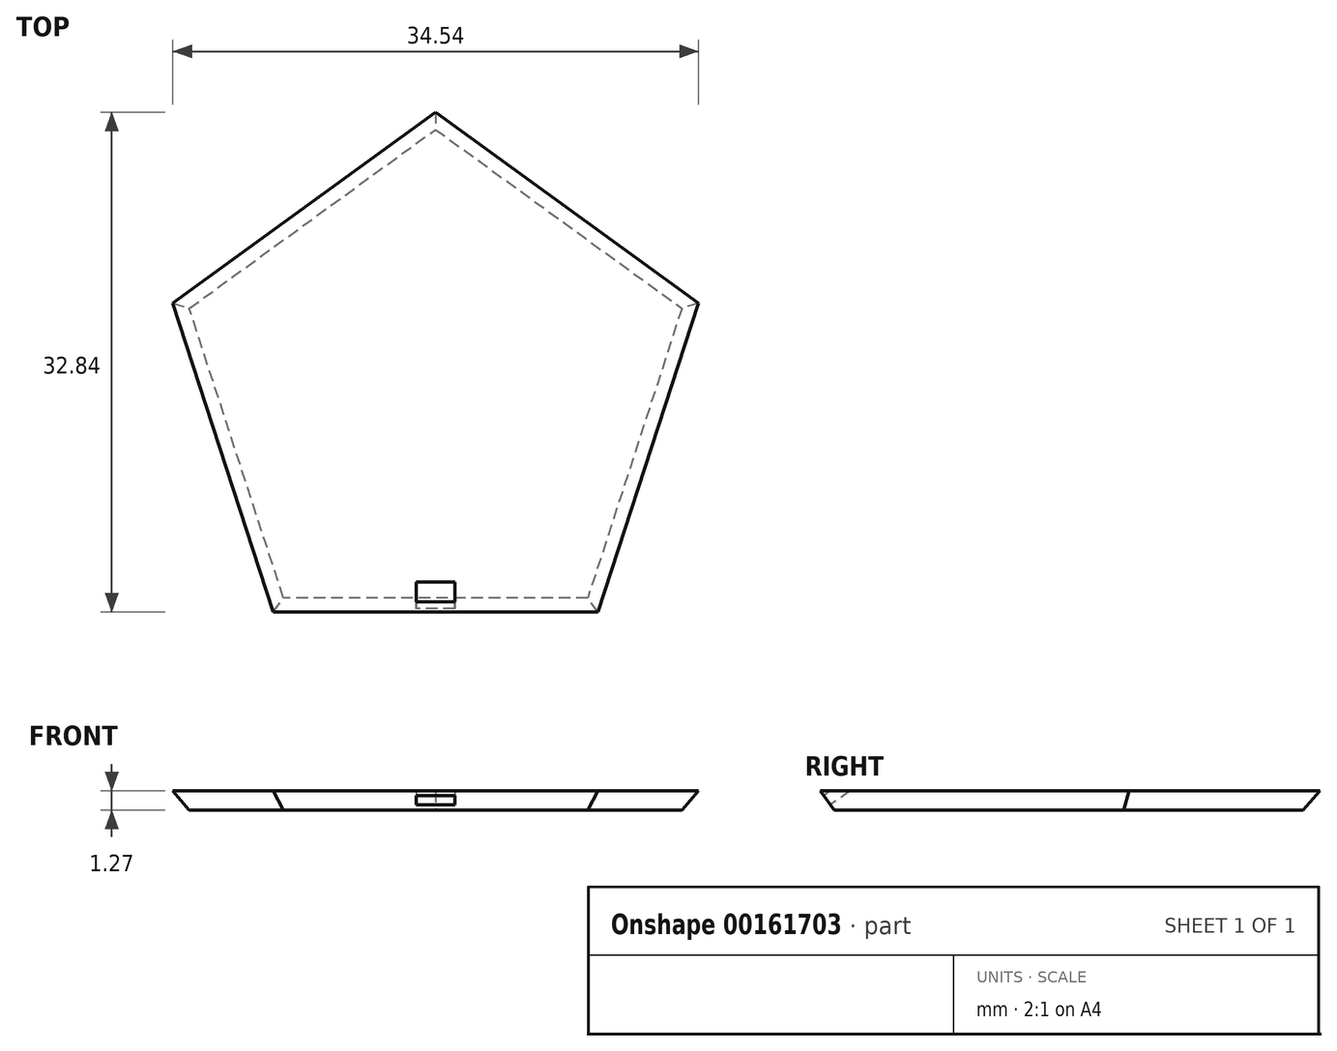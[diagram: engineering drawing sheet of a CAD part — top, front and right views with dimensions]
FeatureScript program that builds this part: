
annotation { "Feature Type Name" : "Feature", "Feature Type Description" : "" }
export const myFeature = defineFeature(function(context is Context, id is Id, definition is map)
    precondition{}
    {
        {
            var Q0;
            Q0=qCreatedBy(makeId("Top.planeOp"),FACE);
            var sketch = newSketch(context, id + "F0", { "sketchPlane" : qUnion([Q0])});
            skCircle(sketch, "E0.cCircle", {"center": v(0, 0) * mm, "radius": 17.01 * mm, "construction": true});
            skLineSegment(sketch, "E0.0", {"start": v(16.18, 5.26) * mm, "end": v(10, -13.76) * mm});
            skLineSegment(sketch, "E0.1", {"start": v(10, -13.76) * mm, "end": v(-10, -13.76) * mm});
            skLineSegment(sketch, "E0.2", {"start": v(-10, -13.76) * mm, "end": v(-16.18, 5.26) * mm});
            skLineSegment(sketch, "E0.3", {"start": v(-16.18, 5.26) * mm, "end": v(0, 17.01) * mm});
            skLineSegment(sketch, "E0.4", {"start": v(0, 17.01) * mm, "end": v(16.18, 5.26) * mm});
            skSolve(sketch);
        }
        {
            var Q0;
            Q0=makeQuery(id+"F0.imprint","IMPRINT",FACE,{"disambiguationData":[TD([[makeQuery(id+"F0.imprint","IMPRINT",EDGE,{"derivedFrom":sQuery(id+"F0.wireOp",EDGE,"E0.0")}),-1.0]])]});
            extrude(context, id + "F1", {"entities" : qUnion([Q0]), "depth" : 1.27 * mm, "hasDraft" : true, "draftAngle" : 36 * degree});
        }
        {
            var Q0;
            Q0=makeQuery(id+"F1.opExtrude","SWEPT_FACE",FACE,{"disambiguationData":[OSD([sQuery(id+"F0.wireOp",EDGE,"E0.1")])]});
            var sketch = newSketch(context, id + "F2", { "sketchPlane" : qUnion([Q0])});
            skLineSegment(sketch, "E1.bottom", {"start": v(1.27, 9.27) * mm, "end": v(-1.27, 9.27) * mm});
            skLineSegment(sketch, "E1.top", {"start": v(1.27, 8.5) * mm, "end": v(-1.27, 8.5) * mm});
            skLineSegment(sketch, "E1.left", {"start": v(1.27, 9.27) * mm, "end": v(1.27, 8.5) * mm});
            skLineSegment(sketch, "E1.right", {"start": v(-1.27, 9.27) * mm, "end": v(-1.27, 8.5) * mm});
            skPoint(sketch, "E1.middle", {"position": v(0, 8.9) * mm});
            skSolve(sketch);
        }
        {
            var Q0;
            Q0=makeQuery(id+"F2.imprint","IMPRINT",FACE,{"disambiguationData":[TD([[makeQuery(id+"F2.imprint","IMPRINT",EDGE,{"derivedFrom":sQuery(id+"F2.wireOp",EDGE,"E1.bottom")}),1.0]])]});
            extrude(context, id + "F3", {"entities" : qUnion([Q0]), "operationType" : NewBodyOperationType.REMOVE, "oppositeDirection" : true, "depth" : 25.4 * mm});
        }
    });
